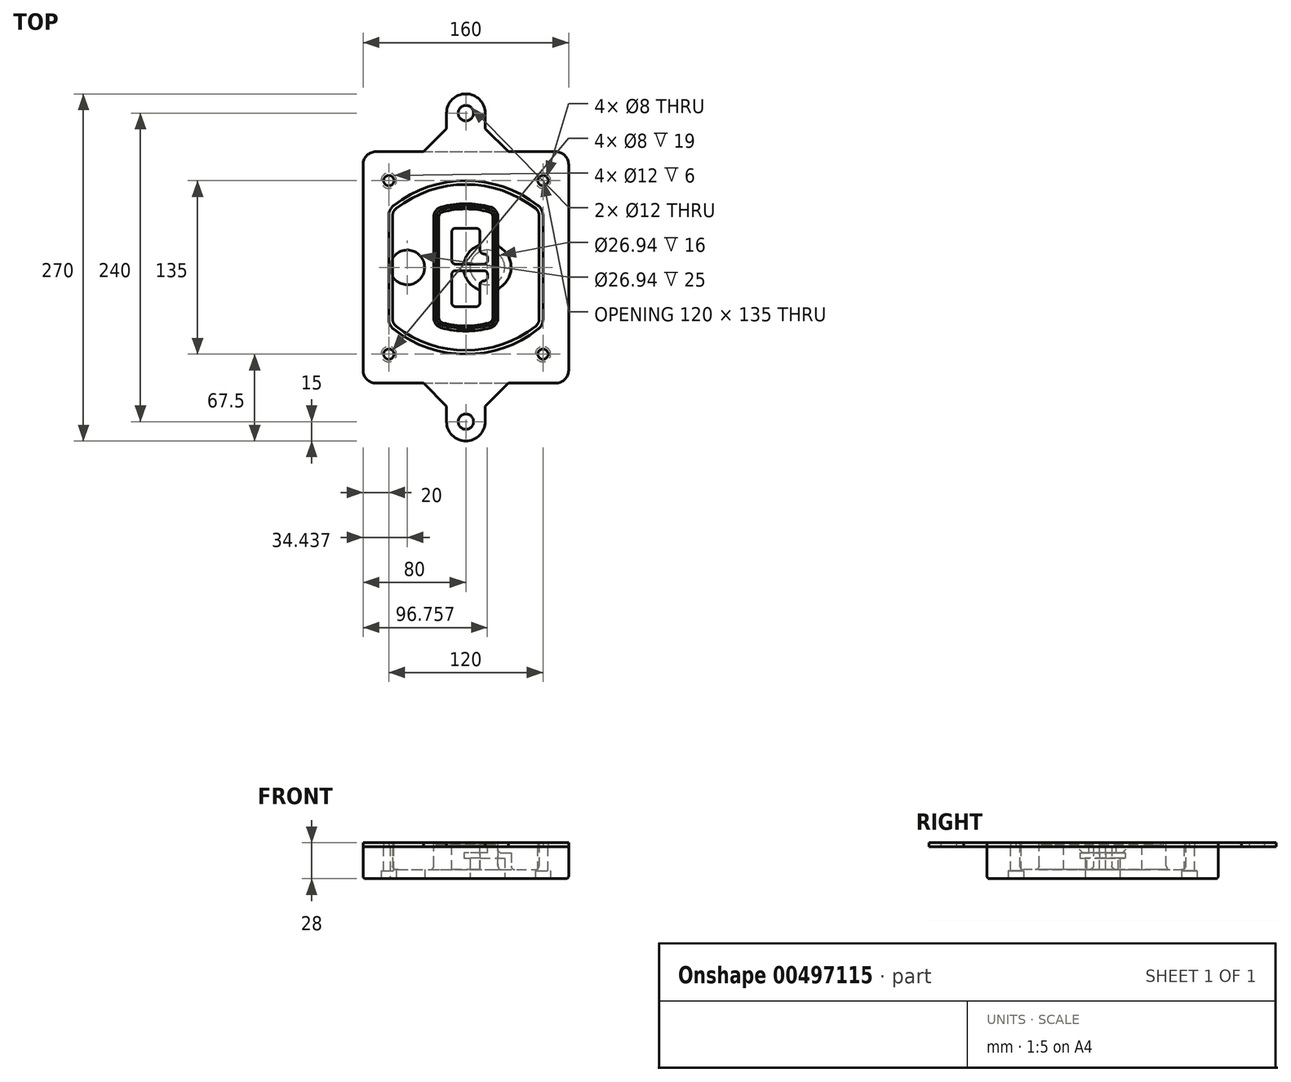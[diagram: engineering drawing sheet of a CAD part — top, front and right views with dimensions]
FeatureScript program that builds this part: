
annotation { "Feature Type Name" : "Feature", "Feature Type Description" : "" }
export const myFeature = defineFeature(function(context is Context, id is Id, definition is map)
    precondition{}
    {
        {
            var Q0;
            Q0=qCreatedBy(makeId("Top.planeOp"),FACE);
            var sketch = newSketch(context, id + "F0", { "sketchPlane" : qUnion([Q0])});
            skPoint(sketch, "E0.rect.middle", {"position": v(0, 0) * mm});
            skLineSegment(sketch, "E1.bottom", {"start": v(-70, -90) * mm, "end": v(70, -90) * mm});
            skLineSegment(sketch, "E1.top", {"start": v(-70, 90) * mm, "end": v(70, 90) * mm});
            skLineSegment(sketch, "E1.left", {"start": v(-80, -80) * mm, "end": v(-80, 80) * mm});
            skLineSegment(sketch, "E1.right", {"start": v(80, -80) * mm, "end": v(80, 80) * mm});
            skLineSegment(sketch, "E2", {"start": v(-80, 90) * mm, "end": v(80, -90) * mm, "construction": true});
            skLineSegment(sketch, "E3", {"start": v(80, 90) * mm, "end": v(-80, -90) * mm, "construction": true});
            skCircle(sketch, "E4", {"center": v(-60, 67.5) * mm, "radius": 4 * mm});
            skCircle(sketch, "E5", {"center": v(60, 67.5) * mm, "radius": 4 * mm});
            skCircle(sketch, "E6", {"center": v(60, -67.5) * mm, "radius": 4 * mm});
            skCircle(sketch, "E7", {"center": v(-60, -67.5) * mm, "radius": 4 * mm});
            skLineSegment(sketch, "E8", {"start": v(-60, 67.5) * mm, "end": v(60, 67.5) * mm, "construction": true});
            skLineSegment(sketch, "E9", {"start": v(60, 67.5) * mm, "end": v(60, -67.5) * mm, "construction": true});
            skLineSegment(sketch, "E10", {"start": v(60, -67.5) * mm, "end": v(-60, -67.5) * mm, "construction": true});
            skLineSegment(sketch, "E11", {"start": v(-60, -67.5) * mm, "end": v(-60, 67.5) * mm, "construction": true});
            skLineSegment(sketch, "E12", {"start": v(-60, 40.3) * mm, "end": v(-60, -40.3) * mm});
            skLineSegment(sketch, "E13", {"start": v(60, 40.3) * mm, "end": v(60, -40.3) * mm});
            skArc(sketch, "E14", {"start": v(56.15, 48.18) * mm, "mid": v(0, 67.5) * mm, "end": v(-56.15, 48.18) * mm});
            skArc(sketch, "E15", {"start": v(-56.15, -48.18) * mm, "mid": v(0, -67.5) * mm, "end": v(56.15, -48.18) * mm});
            skLineSegment(sketch, "E16", {"start": v(-60, 0) * mm, "end": v(60, 0) * mm, "construction": true});
            skPoint(sketch, "E17.visualSharp", {"position": v(-60, -45) * mm});
            skArc(sketch, "E17.filletArc", {"start": v(-60, -40.3) * mm, "mid": v(-58.99, -44.68) * mm, "end": v(-56.15, -48.18) * mm});
            skPoint(sketch, "E18.visualSharp", {"position": v(-60, 45) * mm});
            skArc(sketch, "E18.filletArc", {"start": v(-56.15, 48.18) * mm, "mid": v(-58.99, 44.68) * mm, "end": v(-60, 40.3) * mm});
            skPoint(sketch, "E19.visualSharp", {"position": v(60, 45) * mm});
            skArc(sketch, "E19.filletArc", {"start": v(60, 40.3) * mm, "mid": v(58.99, 44.68) * mm, "end": v(56.15, 48.18) * mm});
            skPoint(sketch, "E20.visualSharp", {"position": v(60, -45) * mm});
            skArc(sketch, "E20.filletArc", {"start": v(56.15, -48.18) * mm, "mid": v(58.99, -44.68) * mm, "end": v(60, -40.3) * mm});
            skPoint(sketch, "E21.visualSharp", {"position": v(-80, 90) * mm});
            skArc(sketch, "E21.filletArc", {"start": v(-70, 90) * mm, "mid": v(-77.07, 87.07) * mm, "end": v(-80, 80) * mm});
            skPoint(sketch, "E22.visualSharp", {"position": v(80, 90) * mm});
            skArc(sketch, "E22.filletArc", {"start": v(80, 80) * mm, "mid": v(77.07, 87.07) * mm, "end": v(70, 90) * mm});
            skPoint(sketch, "E23.visualSharp", {"position": v(80, -90) * mm});
            skArc(sketch, "E23.filletArc", {"start": v(70, -90) * mm, "mid": v(77.07, -87.07) * mm, "end": v(80, -80) * mm});
            skPoint(sketch, "E24.visualSharp", {"position": v(-80, -90) * mm});
            skArc(sketch, "E24.filletArc", {"start": v(-80, -80) * mm, "mid": v(-77.07, -87.07) * mm, "end": v(-70, -90) * mm});
            skArc(sketch, "E25.0", {"start": v(57, 40.3) * mm, "mid": v(56.3, 43.36) * mm, "end": v(54.3, 45.81) * mm});
            skLineSegment(sketch, "E25.1", {"start": v(57, 40.3) * mm, "end": v(57, -40.3) * mm});
            skArc(sketch, "E25.2", {"start": v(54.3, -45.81) * mm, "mid": v(56.3, -43.36) * mm, "end": v(57, -40.3) * mm});
            skArc(sketch, "E25.3", {"start": v(-54.3, -45.81) * mm, "mid": v(0, -64.5) * mm, "end": v(54.3, -45.81) * mm});
            skArc(sketch, "E25.4", {"start": v(-57, -40.3) * mm, "mid": v(-56.3, -43.36) * mm, "end": v(-54.3, -45.81) * mm});
            skArc(sketch, "E25.5", {"start": v(54.3, 45.81) * mm, "mid": v(0, 64.5) * mm, "end": v(-54.3, 45.81) * mm});
            skLineSegment(sketch, "E25.6", {"start": v(-57, 40.3) * mm, "end": v(-57, -40.3) * mm});
            skArc(sketch, "E25.7", {"start": v(-54.3, 45.81) * mm, "mid": v(-56.3, 43.36) * mm, "end": v(-57, 40.3) * mm});
            skArc(sketch, "E26.0", {"start": v(-58.62, 51.33) * mm, "mid": v(-62.58, 46.43) * mm, "end": v(-64, 40.3) * mm});
            skArc(sketch, "E26.1", {"start": v(58.62, 51.33) * mm, "mid": v(0, 71.5) * mm, "end": v(-58.62, 51.33) * mm});
            skArc(sketch, "E26.2", {"start": v(64, 40.3) * mm, "mid": v(62.58, 46.43) * mm, "end": v(58.62, 51.33) * mm});
            skLineSegment(sketch, "E26.3", {"start": v(64, 40.3) * mm, "end": v(64, -40.3) * mm});
            skArc(sketch, "E26.4", {"start": v(58.62, -51.33) * mm, "mid": v(62.58, -46.43) * mm, "end": v(64, -40.3) * mm});
            skLineSegment(sketch, "E26.5", {"start": v(-64, 40.3) * mm, "end": v(-64, -40.3) * mm});
            skArc(sketch, "E26.6", {"start": v(-58.62, -51.33) * mm, "mid": v(0, -71.5) * mm, "end": v(58.62, -51.33) * mm});
            skArc(sketch, "E26.7", {"start": v(-64, -40.3) * mm, "mid": v(-62.58, -46.43) * mm, "end": v(-58.62, -51.33) * mm});
            skSolve(sketch);
        }
        {
            var Q0;
            Q0=makeQuery(id+"F0.imprint","IMPRINT",FACE,{"disambiguationData":[TD([[makeQuery(id+"F0.imprint","IMPRINT",EDGE,{"derivedFrom":sQuery(id+"F0.wireOp",EDGE,"E1.bottom")}),1.0]])]});
            var Q1;
            Q1=makeQuery(id+"F0.imprint","IMPRINT",FACE,{"disambiguationData":[TD([[makeQuery(id+"F0.imprint","IMPRINT",EDGE,{"derivedFrom":sQuery(id+"F0.wireOp",EDGE,"E12")}),1.0]])]});
            var Q2;
            Q2=makeQuery(id+"F0.imprint","IMPRINT",FACE,{"disambiguationData":[TD([[makeQuery(id+"F0.imprint","IMPRINT",EDGE,{"derivedFrom":sQuery(id+"F0.wireOp",EDGE,"E25.0")}),1.0]])]});
            var Q3;
            Q3=makeQuery(id+"F0.imprint","IMPRINT",FACE,{"disambiguationData":[TD([[makeQuery(id+"F0.imprint","IMPRINT",EDGE,{"derivedFrom":sQuery(id+"F0.wireOp",EDGE,"E12")}),-1.0]])]});
            extrude(context, id + "F1", {"entities" : qUnion([Q0, Q1, Q2, Q3]), "oppositeDirection" : true, "depth" : 25 * mm});
        }
        {
            var Q0;
            Q0=makeQuery(id+"F0.imprint","IMPRINT",FACE,{"disambiguationData":[TD([[makeQuery(id+"F0.imprint","IMPRINT",EDGE,{"derivedFrom":sQuery(id+"F0.wireOp",EDGE,"E12")}),1.0]])]});
            extrude(context, id + "F2", {"entities" : qUnion([Q0]), "operationType" : NewBodyOperationType.ADD, "depth" : 3 * mm});
        }
        {
            var Q0;
            Q0=makeQuery(id+"F0.imprint","IMPRINT",FACE,{"disambiguationData":[TD([[makeQuery(id+"F0.imprint","IMPRINT",EDGE,{"derivedFrom":sQuery(id+"F0.wireOp",EDGE,"E25.0")}),1.0]])]});
            extrude(context, id + "F3", {"entities" : qUnion([Q0]), "operationType" : NewBodyOperationType.REMOVE, "oppositeDirection" : true, "depth" : 18 * mm});
        }
        {
            var Q0;
            Q0=makeQuery(id+"F2.opExtrude","CAP_FACE",FACE,{"disambiguationData":[OSD([sQuery(id+"F0.wireOp",EDGE,"E12"),sQuery(id+"F0.wireOp",EDGE,"E13"),sQuery(id+"F0.wireOp",EDGE,"E14"),sQuery(id+"F0.wireOp",EDGE,"E15"),sQuery(id+"F0.wireOp",EDGE,"E17.filletArc"),sQuery(id+"F0.wireOp",EDGE,"E18.filletArc"),sQuery(id+"F0.wireOp",EDGE,"E19.filletArc"),sQuery(id+"F0.wireOp",EDGE,"E20.filletArc"),sQuery(id+"F0.wireOp",EDGE,"E25.0"),sQuery(id+"F0.wireOp",EDGE,"E25.1"),sQuery(id+"F0.wireOp",EDGE,"E25.2"),sQuery(id+"F0.wireOp",EDGE,"E25.3"),sQuery(id+"F0.wireOp",EDGE,"E25.4"),sQuery(id+"F0.wireOp",EDGE,"E25.5"),sQuery(id+"F0.wireOp",EDGE,"E25.6"),sQuery(id+"F0.wireOp",EDGE,"E25.7")])],"isStart":false});
            var sketch = newSketch(context, id + "F4", { "sketchPlane" : qUnion([Q0])});
            skArc(sketch, "E27.0", {"start": v(-19.08, -46.97) * mm, "mid": v(0, -49.5) * mm, "end": v(19.08, -46.97) * mm});
            skArc(sketch, "E28.0", {"start": v(19.08, 46.97) * mm, "mid": v(0, 49.5) * mm, "end": v(-19.08, 46.97) * mm});
            skLineSegment(sketch, "E29", {"start": v(-25, 39.25) * mm, "end": v(-25, -39.25) * mm});
            skLineSegment(sketch, "E30", {"start": v(25, 39.25) * mm, "end": v(25, -39.25) * mm});
            skLineSegment(sketch, "E31", {"start": v(-25, 45.1) * mm, "end": v(25, 45.1) * mm, "construction": true});
            skLineSegment(sketch, "E32", {"start": v(-25, -45.1) * mm, "end": v(25, -45.1) * mm, "construction": true});
            skPoint(sketch, "E33.visualSharp", {"position": v(-25, 45.1) * mm});
            skArc(sketch, "E33.filletArc", {"start": v(-19.08, 46.97) * mm, "mid": v(-23.35, 44.11) * mm, "end": v(-25, 39.25) * mm});
            skPoint(sketch, "E34.visualSharp", {"position": v(25, 45.1) * mm});
            skArc(sketch, "E34.filletArc", {"start": v(25, 39.25) * mm, "mid": v(23.35, 44.11) * mm, "end": v(19.08, 46.97) * mm});
            skPoint(sketch, "E35.visualSharp", {"position": v(25, -45.1) * mm});
            skArc(sketch, "E35.filletArc", {"start": v(19.08, -46.97) * mm, "mid": v(23.35, -44.11) * mm, "end": v(25, -39.25) * mm});
            skPoint(sketch, "E36.visualSharp", {"position": v(-25, -45.1) * mm});
            skArc(sketch, "E36.filletArc", {"start": v(-25, -39.25) * mm, "mid": v(-23.35, -44.11) * mm, "end": v(-19.08, -46.97) * mm});
            skArc(sketch, "E37.0", {"start": v(54.3, 45.81) * mm, "mid": v(0, 64.5) * mm, "end": v(-54.3, 45.81) * mm});
            skArc(sketch, "E37.1", {"start": v(-54.3, 45.81) * mm, "mid": v(-56.3, 43.36) * mm, "end": v(-57, 40.3) * mm});
            skLineSegment(sketch, "E37.2", {"start": v(-57, 40.3) * mm, "end": v(-57, -40.3) * mm});
            skArc(sketch, "E37.3", {"start": v(-57, -40.3) * mm, "mid": v(-56.3, -43.36) * mm, "end": v(-54.3, -45.81) * mm});
            skArc(sketch, "E37.4", {"start": v(-54.3, -45.81) * mm, "mid": v(0, -64.5) * mm, "end": v(54.3, -45.81) * mm});
            skArc(sketch, "E37.5", {"start": v(54.3, -45.81) * mm, "mid": v(56.3, -43.36) * mm, "end": v(57, -40.3) * mm});
            skLineSegment(sketch, "E37.6", {"start": v(57, 40.3) * mm, "end": v(57, -40.3) * mm});
            skArc(sketch, "E37.7", {"start": v(57, 40.3) * mm, "mid": v(56.3, 43.36) * mm, "end": v(54.3, 45.81) * mm});
            skLineSegment(sketch, "E38.0", {"start": v(23, 39.25) * mm, "end": v(23, -39.25) * mm});
            skArc(sketch, "E38.1", {"start": v(18.56, -45.04) * mm, "mid": v(21.76, -42.9) * mm, "end": v(23, -39.25) * mm});
            skArc(sketch, "E38.2", {"start": v(-18.56, -45.04) * mm, "mid": v(0, -47.5) * mm, "end": v(18.56, -45.04) * mm});
            skArc(sketch, "E38.3", {"start": v(-23, -39.25) * mm, "mid": v(-21.76, -42.9) * mm, "end": v(-18.56, -45.04) * mm});
            skLineSegment(sketch, "E38.4", {"start": v(-23, 39.25) * mm, "end": v(-23, -39.25) * mm});
            skArc(sketch, "E38.5", {"start": v(23, 39.25) * mm, "mid": v(21.76, 42.9) * mm, "end": v(18.56, 45.04) * mm});
            skArc(sketch, "E38.6", {"start": v(-18.56, 45.04) * mm, "mid": v(-21.76, 42.9) * mm, "end": v(-23, 39.25) * mm});
            skArc(sketch, "E38.7", {"start": v(18.56, 45.04) * mm, "mid": v(0, 47.5) * mm, "end": v(-18.56, 45.04) * mm});
            skArc(sketch, "E39.0", {"start": v(21, 39.25) * mm, "mid": v(20.18, 41.68) * mm, "end": v(18.04, 43.1) * mm});
            skLineSegment(sketch, "E39.1", {"start": v(21, 39.25) * mm, "end": v(21, -39.25) * mm});
            skArc(sketch, "E39.2", {"start": v(18.04, -43.1) * mm, "mid": v(20.18, -41.68) * mm, "end": v(21, -39.25) * mm});
            skArc(sketch, "E39.3", {"start": v(-18.04, -43.1) * mm, "mid": v(0, -45.5) * mm, "end": v(18.04, -43.1) * mm});
            skArc(sketch, "E39.4", {"start": v(-21, -39.25) * mm, "mid": v(-20.18, -41.68) * mm, "end": v(-18.04, -43.1) * mm});
            skArc(sketch, "E39.5", {"start": v(18.04, 43.1) * mm, "mid": v(0, 45.5) * mm, "end": v(-18.04, 43.1) * mm});
            skLineSegment(sketch, "E39.6", {"start": v(-21, 39.25) * mm, "end": v(-21, -39.25) * mm});
            skArc(sketch, "E39.7", {"start": v(-18.04, 43.1) * mm, "mid": v(-20.18, 41.68) * mm, "end": v(-21, 39.25) * mm});
            skLineSegment(sketch, "E40", {"start": v(-25, 0) * mm, "end": v(25, 0) * mm, "construction": true});
            skLineSegment(sketch, "E41", {"start": v(-11, 5.5) * mm, "end": v(-11, 27.5) * mm});
            skLineSegment(sketch, "E42", {"start": v(-8, 30.5) * mm, "end": v(8, 30.5) * mm});
            skLineSegment(sketch, "E43", {"start": v(11, 27.5) * mm, "end": v(11, 13.5) * mm});
            skLineSegment(sketch, "E44", {"start": v(14, 10.5) * mm, "end": v(14, 10.5) * mm});
            skLineSegment(sketch, "E45", {"start": v(17, 7.5) * mm, "end": v(17, 5.5) * mm});
            skLineSegment(sketch, "E46", {"start": v(14, 2.5) * mm, "end": v(-8, 2.5) * mm});
            skPoint(sketch, "E47.visualSharp", {"position": v(-11, 30.5) * mm});
            skArc(sketch, "E47.filletArc", {"start": v(-8, 30.5) * mm, "mid": v(-10.12, 29.62) * mm, "end": v(-11, 27.5) * mm});
            skPoint(sketch, "E48.visualSharp", {"position": v(11, 30.5) * mm});
            skArc(sketch, "E48.filletArc", {"start": v(11, 27.5) * mm, "mid": v(10.12, 29.62) * mm, "end": v(8, 30.5) * mm});
            skPoint(sketch, "E49.visualSharp", {"position": v(11, 10.5) * mm});
            skArc(sketch, "E49.filletArc", {"start": v(11, 13.5) * mm, "mid": v(11.88, 11.38) * mm, "end": v(14, 10.5) * mm});
            skPoint(sketch, "E50.visualSharp", {"position": v(17, 10.5) * mm});
            skArc(sketch, "E50.filletArc", {"start": v(17, 7.5) * mm, "mid": v(16.12, 9.62) * mm, "end": v(14, 10.5) * mm});
            skPoint(sketch, "E51.visualSharp", {"position": v(17, 2.5) * mm});
            skArc(sketch, "E51.filletArc", {"start": v(14, 2.5) * mm, "mid": v(16.12, 3.38) * mm, "end": v(17, 5.5) * mm});
            skPoint(sketch, "E52.visualSharp", {"position": v(-11, 2.5) * mm});
            skArc(sketch, "E52.filletArc", {"start": v(-11, 5.5) * mm, "mid": v(-10.12, 3.38) * mm, "end": v(-8, 2.5) * mm});
            skLineSegment(sketch, "E53.0.MirrorCS", {"start": v(14, -2.5) * mm, "end": v(-8, -2.5) * mm});
            skArc(sketch, "E54.0.MirrorCS", {"start": v(-11, -5.5) * mm, "mid": v(-10.12, -3.38) * mm, "end": v(-8, -2.5) * mm});
            skLineSegment(sketch, "E55.0.MirrorCS", {"start": v(-11, -5.5) * mm, "end": v(-11, -27.5) * mm});
            skArc(sketch, "E56.0.MirrorCS", {"start": v(-8, -30.5) * mm, "mid": v(-10.12, -29.62) * mm, "end": v(-11, -27.5) * mm});
            skLineSegment(sketch, "E57.0.MirrorCS", {"start": v(-8, -30.5) * mm, "end": v(8, -30.5) * mm});
            skArc(sketch, "E58.0.MirrorCS", {"start": v(11, -27.5) * mm, "mid": v(10.12, -29.62) * mm, "end": v(8, -30.5) * mm});
            skLineSegment(sketch, "E59.0.MirrorCS", {"start": v(11, -27.5) * mm, "end": v(11, -13.5) * mm});
            skArc(sketch, "E60.0.MirrorCS", {"start": v(11, -13.5) * mm, "mid": v(11.88, -11.38) * mm, "end": v(14, -10.5) * mm});
            skArc(sketch, "E61.0.MirrorCS", {"start": v(17, -7.5) * mm, "mid": v(16.12, -9.62) * mm, "end": v(14, -10.5) * mm});
            skLineSegment(sketch, "E62.0.MirrorCS", {"start": v(17, -7.5) * mm, "end": v(17, -5.5) * mm});
            skArc(sketch, "E63.0.MirrorCS", {"start": v(14, -2.5) * mm, "mid": v(16.12, -3.38) * mm, "end": v(17, -5.5) * mm});
            skSolve(sketch);
        }
        {
            var Q0;
            Q0=makeQuery(id+"F4.imprint","IMPRINT",FACE,{"disambiguationData":[TD([[makeQuery(id+"F4.imprint","IMPRINT",EDGE,{"derivedFrom":sQuery(id+"F4.wireOp",EDGE,"E27.0")}),1.0]])]});
            var Q1;
            Q1=makeQuery(id+"F4.imprint","IMPRINT",FACE,{"disambiguationData":[TD([[makeQuery(id+"F4.imprint","IMPRINT",EDGE,{"derivedFrom":sQuery(id+"F4.wireOp",EDGE,"E38.0")}),-1.0]])]});
            var Q2;
            Q2=makeQuery(id+"F4.imprint","IMPRINT",FACE,{"disambiguationData":[TD([[makeQuery(id+"F4.imprint","IMPRINT",EDGE,{"derivedFrom":sQuery(id+"F4.wireOp",EDGE,"E39.0")}),1.0]])]});
            extrude(context, id + "F5", {"entities" : qUnion([Q0, Q1, Q2]), "operationType" : NewBodyOperationType.ADD, "endBound" : BoundingType.UP_TO_NEXT, "oppositeDirection" : true, "depth" : 25 * mm});
        }
        {
            var Q0;
            Q0=makeQuery(id+"F4.imprint","IMPRINT",FACE,{"disambiguationData":[TD([[makeQuery(id+"F4.imprint","IMPRINT",EDGE,{"derivedFrom":sQuery(id+"F4.wireOp",EDGE,"E38.0")}),-1.0]])]});
            extrude(context, id + "F6", {"entities" : qUnion([Q0]), "operationType" : NewBodyOperationType.REMOVE, "oppositeDirection" : true, "depth" : 2 * mm});
        }
        {
            var Q0;
            Q0=makeQuery(id+"F1.opExtrude","CAP_FACE",FACE,{"disambiguationData":[OSD([sQuery(id+"F0.wireOp",EDGE,"E1.bottom"),sQuery(id+"F0.wireOp",EDGE,"E1.top"),sQuery(id+"F0.wireOp",EDGE,"E1.left"),sQuery(id+"F0.wireOp",EDGE,"E1.right"),sQuery(id+"F0.wireOp",EDGE,"E4"),sQuery(id+"F0.wireOp",EDGE,"E5"),sQuery(id+"F0.wireOp",EDGE,"E6"),sQuery(id+"F0.wireOp",EDGE,"E7"),sQuery(id+"F0.wireOp",EDGE,"E21.filletArc"),sQuery(id+"F0.wireOp",EDGE,"E22.filletArc"),sQuery(id+"F0.wireOp",EDGE,"E23.filletArc"),sQuery(id+"F0.wireOp",EDGE,"E24.filletArc")])],"isStart":false});
            var sketch = newSketch(context, id + "F7", { "sketchPlane" : qUnion([Q0])});
            skCircle(sketch, "E64", {"center": v(16.76, 0) * mm, "radius": 13.47 * mm});
            skCircle(sketch, "E65", {"center": v(-45.56, 0) * mm, "radius": 13.47 * mm});
            skLineSegment(sketch, "E66", {"start": v(80, 0) * mm, "end": v(-80, 0) * mm});
            skCircle(sketch, "E67", {"center": v(16.76, 0) * mm, "radius": 18.47 * mm});
            skCircle(sketch, "E68", {"center": v(60, -67.5) * mm, "radius": 6 * mm});
            skCircle(sketch, "E69", {"center": v(-60, -67.5) * mm, "radius": 6 * mm});
            skCircle(sketch, "E70", {"center": v(-60, 67.5) * mm, "radius": 6 * mm});
            skCircle(sketch, "E71", {"center": v(60, 67.5) * mm, "radius": 6 * mm});
            skSolve(sketch);
        }
        {
            var Q0;
            {var subQ1=sQuery(id+"F7.wireOp",EDGE,"E66");var subQ4=sQuery(id+"F7.wireOp",EDGE,"E64");var subQ6=makeQuery(id+"F7.imprint","INTERSECT",VERTEX,{"disambiguationData":[OD(0.0)],"derivedFrom":[subQ4,subQ1]});Q0=makeQuery(id+"F7.imprint","IMPRINT",FACE,{"disambiguationData":[TD([[makeQuery(id+"F7.imprint","IMPRINT",EDGE,{"disambiguationData":[TD([[subQ6,-1.0]])],"derivedFrom":subQ4}),-1.0]])]});}
            var Q1;
            {var subQ0=sQuery(id+"F7.wireOp",EDGE,"E66");var subQ1=sQuery(id+"F7.wireOp",EDGE,"E64");var subQ3=makeQuery(id+"F7.imprint","INTERSECT",VERTEX,{"disambiguationData":[OD(0.0)],"derivedFrom":[subQ1,subQ0]});Q1=makeQuery(id+"F7.imprint","IMPRINT",FACE,{"disambiguationData":[TD([[makeQuery(id+"F7.imprint","IMPRINT",EDGE,{"disambiguationData":[TD([[subQ3,-1.0]])],"derivedFrom":subQ1}),1.0]])]});}
            var Q2;
            {var subQ0=sQuery(id+"F7.wireOp",EDGE,"E66");var subQ1=sQuery(id+"F7.wireOp",EDGE,"E64");var subQ3=makeQuery(id+"F7.imprint","INTERSECT",VERTEX,{"disambiguationData":[OD(0.0)],"derivedFrom":[subQ1,subQ0]});Q2=makeQuery(id+"F7.imprint","IMPRINT",FACE,{"disambiguationData":[TD([[makeQuery(id+"F7.imprint","IMPRINT",EDGE,{"disambiguationData":[TD([[subQ3,1.0]])],"derivedFrom":subQ1}),1.0]])]});}
            var Q3;
            {var subQ1=sQuery(id+"F7.wireOp",EDGE,"E66");var subQ4=sQuery(id+"F7.wireOp",EDGE,"E64");var subQ6=makeQuery(id+"F7.imprint","INTERSECT",VERTEX,{"disambiguationData":[OD(0.0)],"derivedFrom":[subQ4,subQ1]});Q3=makeQuery(id+"F7.imprint","IMPRINT",FACE,{"disambiguationData":[TD([[makeQuery(id+"F7.imprint","IMPRINT",EDGE,{"disambiguationData":[TD([[subQ6,1.0]])],"derivedFrom":subQ4}),-1.0]])]});}
            extrude(context, id + "F8", {"entities" : qUnion([Q0, Q1, Q2, Q3]), "operationType" : NewBodyOperationType.ADD, "oppositeDirection" : true, "depth" : 20 * mm});
        }
        {
            var Q0;
            {var subQ0=sQuery(id+"F7.wireOp",EDGE,"E66");var subQ1=sQuery(id+"F7.wireOp",EDGE,"E64");var subQ3=makeQuery(id+"F7.imprint","INTERSECT",VERTEX,{"disambiguationData":[OD(0.0)],"derivedFrom":[subQ1,subQ0]});Q0=makeQuery(id+"F7.imprint","IMPRINT",FACE,{"disambiguationData":[TD([[makeQuery(id+"F7.imprint","IMPRINT",EDGE,{"disambiguationData":[TD([[subQ3,-1.0]])],"derivedFrom":subQ1}),1.0]])]});}
            var Q1;
            {var subQ0=sQuery(id+"F7.wireOp",EDGE,"E66");var subQ1=sQuery(id+"F7.wireOp",EDGE,"E64");var subQ3=makeQuery(id+"F7.imprint","INTERSECT",VERTEX,{"disambiguationData":[OD(0.0)],"derivedFrom":[subQ1,subQ0]});Q1=makeQuery(id+"F7.imprint","IMPRINT",FACE,{"disambiguationData":[TD([[makeQuery(id+"F7.imprint","IMPRINT",EDGE,{"disambiguationData":[TD([[subQ3,1.0]])],"derivedFrom":subQ1}),1.0]])]});}
            extrude(context, id + "F9", {"entities" : qUnion([Q0, Q1]), "operationType" : NewBodyOperationType.REMOVE, "oppositeDirection" : true, "depth" : 16 * mm});
        }
        {
            var Q0;
            {var subQ0=sQuery(id+"F7.wireOp",EDGE,"E66");var subQ1=sQuery(id+"F7.wireOp",EDGE,"E65");var subQ3=makeQuery(id+"F7.imprint","INTERSECT",VERTEX,{"disambiguationData":[OD(0.0)],"derivedFrom":[subQ1,subQ0]});Q0=makeQuery(id+"F7.imprint","IMPRINT",FACE,{"disambiguationData":[TD([[makeQuery(id+"F7.imprint","IMPRINT",EDGE,{"disambiguationData":[TD([[subQ3,-1.0]])],"derivedFrom":subQ1}),1.0]])]});}
            var Q1;
            {var subQ0=sQuery(id+"F7.wireOp",EDGE,"E66");var subQ1=sQuery(id+"F7.wireOp",EDGE,"E65");var subQ3=makeQuery(id+"F7.imprint","INTERSECT",VERTEX,{"disambiguationData":[OD(0.0)],"derivedFrom":[subQ1,subQ0]});Q1=makeQuery(id+"F7.imprint","IMPRINT",FACE,{"disambiguationData":[TD([[makeQuery(id+"F7.imprint","IMPRINT",EDGE,{"disambiguationData":[TD([[subQ3,1.0]])],"derivedFrom":subQ1}),1.0]])]});}
            extrude(context, id + "F10", {"entities" : qUnion([Q0, Q1]), "operationType" : NewBodyOperationType.REMOVE, "oppositeDirection" : true, "depth" : 25 * mm});
        }
        {
            var Q0;
            Q0=makeQuery(id+"F7.imprint","IMPRINT",FACE,{"disambiguationData":[TD([[makeQuery(id+"F7.imprint","IMPRINT",EDGE,{"derivedFrom":sQuery(id+"F7.wireOp",EDGE,"E68")}),1.0]])]});
            var Q1;
            Q1=makeQuery(id+"F7.imprint","IMPRINT",FACE,{"disambiguationData":[TD([[makeQuery(id+"F7.imprint","IMPRINT",EDGE,{"derivedFrom":makeQuery(id+"F1.opExtrude","CAP_EDGE",EDGE,{"disambiguationData":[OSD([sQuery(id+"F0.wireOp",EDGE,"E5")])],"isStart":false})}),-1.0]])]});
            var Q2;
            Q2=makeQuery(id+"F7.imprint","IMPRINT",FACE,{"disambiguationData":[TD([[makeQuery(id+"F7.imprint","IMPRINT",EDGE,{"derivedFrom":sQuery(id+"F7.wireOp",EDGE,"E69")}),1.0]])]});
            var Q3;
            Q3=makeQuery(id+"F7.imprint","IMPRINT",FACE,{"disambiguationData":[TD([[makeQuery(id+"F7.imprint","IMPRINT",EDGE,{"derivedFrom":makeQuery(id+"F1.opExtrude","CAP_EDGE",EDGE,{"disambiguationData":[OSD([sQuery(id+"F0.wireOp",EDGE,"E4")])],"isStart":false})}),-1.0]])]});
            var Q4;
            Q4=makeQuery(id+"F7.imprint","IMPRINT",FACE,{"disambiguationData":[TD([[makeQuery(id+"F7.imprint","IMPRINT",EDGE,{"derivedFrom":sQuery(id+"F7.wireOp",EDGE,"E70")}),1.0]])]});
            var Q5;
            Q5=makeQuery(id+"F7.imprint","IMPRINT",FACE,{"disambiguationData":[TD([[makeQuery(id+"F7.imprint","IMPRINT",EDGE,{"derivedFrom":makeQuery(id+"F1.opExtrude","CAP_EDGE",EDGE,{"disambiguationData":[OSD([sQuery(id+"F0.wireOp",EDGE,"E7")])],"isStart":false})}),-1.0]])]});
            var Q6;
            Q6=makeQuery(id+"F7.imprint","IMPRINT",FACE,{"disambiguationData":[TD([[makeQuery(id+"F7.imprint","IMPRINT",EDGE,{"derivedFrom":sQuery(id+"F7.wireOp",EDGE,"E71")}),1.0]])]});
            var Q7;
            Q7=makeQuery(id+"F7.imprint","IMPRINT",FACE,{"disambiguationData":[TD([[makeQuery(id+"F7.imprint","IMPRINT",EDGE,{"derivedFrom":makeQuery(id+"F1.opExtrude","CAP_EDGE",EDGE,{"disambiguationData":[OSD([sQuery(id+"F0.wireOp",EDGE,"E6")])],"isStart":false})}),-1.0]])]});
            extrude(context, id + "F11", {"entities" : qUnion([Q0, Q1, Q2, Q3, Q4, Q5, Q6, Q7]), "operationType" : NewBodyOperationType.REMOVE, "oppositeDirection" : true, "depth" : 6 * mm});
        }
        {
            var Q0;
            Q0=makeQuery(id+"F9.boolean.opBoolean","COPY",FACE,{"derivedFrom":makeQuery(id+"F9.opExtrude","CAP_FACE",FACE,{"disambiguationData":[OSD([sQuery(id+"F7.wireOp",EDGE,"E64")])],"isStart":false})});
            var sketch = newSketch(context, id + "F12", { "sketchPlane" : qUnion([Q0])});
            skArc(sketch, "E72.0", {"start": v(11, 17.55) * mm, "mid": v(2.57, 11.82) * mm, "end": v(-1.54, 2.5) * mm});
            skArc(sketch, "E72.1", {"start": v(-1.54, -2.5) * mm, "mid": v(2.57, -11.82) * mm, "end": v(11, -17.55) * mm});
            skLineSegment(sketch, "E73", {"start": v(-1.54, -2.5) * mm, "end": v(14, -2.5) * mm});
            skLineSegment(sketch, "E74.0", {"start": v(14, 2.5) * mm, "end": v(-1.54, 2.5) * mm});
            skArc(sketch, "E74.1", {"start": v(14, 2.5) * mm, "mid": v(16.12, 3.38) * mm, "end": v(17, 5.5) * mm});
            skLineSegment(sketch, "E74.2", {"start": v(17, 7.5) * mm, "end": v(17, 5.5) * mm});
            skArc(sketch, "E74.3", {"start": v(17, 7.5) * mm, "mid": v(16.12, 9.62) * mm, "end": v(14, 10.5) * mm});
            skArc(sketch, "E74.4", {"start": v(11, 13.5) * mm, "mid": v(11.88, 11.38) * mm, "end": v(14, 10.5) * mm});
            skLineSegment(sketch, "E74.5", {"start": v(11, 17.55) * mm, "end": v(11, 13.5) * mm});
            skLineSegment(sketch, "E74.7", {"start": v(14, -2.5) * mm, "end": v(-1.54, -2.5) * mm});
            skArc(sketch, "E74.8", {"start": v(14, -2.5) * mm, "mid": v(16.12, -3.38) * mm, "end": v(17, -5.5) * mm});
            skLineSegment(sketch, "E74.9", {"start": v(17, -7.5) * mm, "end": v(17, -5.5) * mm});
            skArc(sketch, "E74.10", {"start": v(17, -7.5) * mm, "mid": v(16.12, -9.62) * mm, "end": v(14, -10.5) * mm});
            skArc(sketch, "E74.11", {"start": v(11, -13.5) * mm, "mid": v(11.88, -11.38) * mm, "end": v(14, -10.5) * mm});
            skLineSegment(sketch, "E74.12", {"start": v(11, -17.55) * mm, "end": v(11, -13.5) * mm});
            skPoint(sketch, "E75.orphan", {"position": v(11, -27.5) * mm});
            skPoint(sketch, "E76.orphan", {"position": v(-8, -2.5) * mm});
            skPoint(sketch, "E77.orphan", {"position": v(-8, 2.5) * mm});
            skPoint(sketch, "E78.orphan", {"position": v(11, 27.5) * mm});
            skSolve(sketch);
        }
        {
            var Q0;
            {var subQ7=sQuery(id+"F12.wireOp",EDGE,"E72.0");var subQ14=sQuery(id+"F12.wireOp",EDGE,"E72.1");var subQ16=sQuery(id+"F12.wireOp",EDGE,"E74.1");var subQ18=sQuery(id+"F12.wireOp",EDGE,"E74.8");Q0=qUnion([makeQuery(id+"F12.imprint","IMPRINT",FACE,{"disambiguationData":[TD([[makeQuery(id+"F12.imprint","IMPRINT",EDGE,{"derivedFrom":subQ7}),1.0]])]}),makeQuery(id+"F12.imprint","IMPRINT",FACE,{"disambiguationData":[TD([[makeQuery(id+"F12.imprint","IMPRINT",EDGE,{"derivedFrom":subQ14}),1.0]])]}),makeQuery(id+"F12.imprint","IMPRINT",FACE,{"disambiguationData":[TD([[makeQuery(id+"F12.imprint","IMPRINT",EDGE,{"derivedFrom":subQ16}),1.0]])]}),makeQuery(id+"F12.imprint","IMPRINT",FACE,{"disambiguationData":[TD([[makeQuery(id+"F12.imprint","IMPRINT",EDGE,{"derivedFrom":subQ18}),-1.0]])]})]);}
            var Q1;
            Q1=makeQuery(id+"F5.boolean.opBoolean","SPLIT",FACE,{"disambiguationData":[TD([makeQuery(id+"F5.opExtrude","SWEPT_FACE",FACE,{"disambiguationData":[OSD([sQuery(id+"F4.wireOp",EDGE,"E41")])]})])],"derivedFrom":makeQuery(id+"F3.boolean.opBoolean","COPY",FACE,{"derivedFrom":makeQuery(id+"F3.opExtrude","CAP_FACE",FACE,{"disambiguationData":[OSD([sQuery(id+"F0.wireOp",EDGE,"E25.0"),sQuery(id+"F0.wireOp",EDGE,"E25.1"),sQuery(id+"F0.wireOp",EDGE,"E25.2"),sQuery(id+"F0.wireOp",EDGE,"E25.3"),sQuery(id+"F0.wireOp",EDGE,"E25.4"),sQuery(id+"F0.wireOp",EDGE,"E25.5"),sQuery(id+"F0.wireOp",EDGE,"E25.6"),sQuery(id+"F0.wireOp",EDGE,"E25.7")])],"isStart":false})})});
            extrude(context, id + "F13", {"entities" : qUnion([Q0]), "operationType" : NewBodyOperationType.REMOVE, "endBound" : BoundingType.UP_TO_SURFACE, "endBoundEntityFace" : qUnion([Q1]), "depth" : 25 * mm});
        }
        {
            var Q0;
            Q0=makeQuery(id+"F3.boolean.opBoolean","COPY",EDGE,{"derivedFrom":makeQuery(id+"F3.opExtrude","CAP_EDGE",EDGE,{"disambiguationData":[OSD([sQuery(id+"F0.wireOp",EDGE,"E25.6")])],"isStart":false})});
            var Q1;
            Q1=makeQuery(id+"F8.boolean.opBoolean","INTERSECT",EDGE,{"derivedFrom":[makeQuery(id+"F5.opExtrude","SWEPT_FACE",FACE,{"disambiguationData":[OSD([sQuery(id+"F4.wireOp",EDGE,"E30")])]}),makeQuery(id+"F8.opExtrude","CAP_FACE",FACE,{"disambiguationData":[OSD([sQuery(id+"F7.wireOp",EDGE,"E67")])],"isStart":false})]});
            var Q2;
            Q2=makeQuery(id+"F8.boolean.opBoolean","INTERSECT",EDGE,{"disambiguationData":[OD(1.0)],"derivedFrom":[makeQuery(id+"F5.opExtrude","SWEPT_FACE",FACE,{"disambiguationData":[OSD([sQuery(id+"F4.wireOp",EDGE,"E30")])]}),makeQuery(id+"F8.opExtrude","SWEPT_FACE",FACE,{"disambiguationData":[OSD([sQuery(id+"F7.wireOp",EDGE,"E67")])]})]});
            var Q3;
            {var subQ0=sQuery(id+"F4.wireOp",EDGE,"E30");Q3=makeQuery(id+"F8.boolean.opBoolean","SPLIT",EDGE,{"disambiguationData":[TD([makeQuery(id+"F5.opExtrude","SWEPT_FACE",FACE,{"disambiguationData":[OSD([sQuery(id+"F4.wireOp",EDGE,"E35.filletArc")])]})])],"derivedFrom":makeQuery(id+"F5.opExtrude","CAP_EDGE",EDGE,{"disambiguationData":[OSD([subQ0])],"isStart":false})});}
            var Q4;
            {var subQ0=sQuery(id+"F0.wireOp",EDGE,"E25.7");var subQ1=sQuery(id+"F0.wireOp",EDGE,"E25.1");var subQ2=sQuery(id+"F0.wireOp",EDGE,"E25.6");var subQ3=sQuery(id+"F0.wireOp",EDGE,"E25.5");var subQ4=sQuery(id+"F0.wireOp",EDGE,"E25.4");var subQ5=sQuery(id+"F0.wireOp",EDGE,"E25.0");var subQ6=sQuery(id+"F0.wireOp",EDGE,"E25.2");var subQ7=sQuery(id+"F0.wireOp",EDGE,"E25.3");Q4=makeQuery(id+"F8.boolean.opBoolean","INTERSECT",EDGE,{"derivedFrom":[makeQuery(id+"F5.boolean.opBoolean","SPLIT",FACE,{"disambiguationData":[TD([makeQuery(id+"F2.opExtrude","SWEPT_FACE",FACE,{"disambiguationData":[OSD([subQ5])]})])],"derivedFrom":makeQuery(id+"F3.boolean.opBoolean","COPY",FACE,{"derivedFrom":makeQuery(id+"F3.opExtrude","CAP_FACE",FACE,{"disambiguationData":[OSD([subQ5,subQ1,subQ6,subQ7,subQ4,subQ3,subQ2,subQ0])],"isStart":false})})}),makeQuery(id+"F8.opExtrude","SWEPT_FACE",FACE,{"disambiguationData":[OSD([sQuery(id+"F7.wireOp",EDGE,"E67")])]})]});}
            var Q5;
            Q5=makeQuery(id+"F8.boolean.opBoolean","INTERSECT",EDGE,{"disambiguationData":[OD(0.0)],"derivedFrom":[makeQuery(id+"F5.opExtrude","SWEPT_FACE",FACE,{"disambiguationData":[OSD([sQuery(id+"F4.wireOp",EDGE,"E30")])]}),makeQuery(id+"F8.opExtrude","SWEPT_FACE",FACE,{"disambiguationData":[OSD([sQuery(id+"F7.wireOp",EDGE,"E67")])]})]});
            fillet(context, id + "F14", {"entities" : qUnion([Q0, Q1, Q2, Q3, Q4, Q5]), "radius" : 3 * mm, "tangentPropagation" : true, "allowEdgeOverflow" : false});
        }
        {
            var Q0;
            Q0=makeQuery(id+"F1.opExtrude","CAP_EDGE",EDGE,{"disambiguationData":[OSD([sQuery(id+"F0.wireOp",EDGE,"E1.bottom")])],"isStart":false});
            fillet(context, id + "F15", {"entities" : qUnion([Q0]), "radius" : 2 * mm, "tangentPropagation" : true, "allowEdgeOverflow" : false});
        }
        {
            var Q0;
            {var subQ0=sQuery(id+"F0.wireOp",EDGE,"E21.filletArc");var subQ1=sQuery(id+"F0.wireOp",EDGE,"E7");var subQ2=sQuery(id+"F0.wireOp",EDGE,"E6");var subQ3=sQuery(id+"F0.wireOp",EDGE,"E5");var subQ4=sQuery(id+"F0.wireOp",EDGE,"E4");var subQ5=sQuery(id+"F0.wireOp",EDGE,"E22.filletArc");var subQ6=sQuery(id+"F0.wireOp",EDGE,"E1.bottom");var subQ7=sQuery(id+"F0.wireOp",EDGE,"E1.right");var subQ8=sQuery(id+"F0.wireOp",EDGE,"E1.top");var subQ9=sQuery(id+"F0.wireOp",EDGE,"E1.left");var subQ10=sQuery(id+"F0.wireOp",EDGE,"E23.filletArc");var subQ11=sQuery(id+"F0.wireOp",EDGE,"E24.filletArc");Q0=makeQuery(id+"F2.boolean.opBoolean","SPLIT",FACE,{"disambiguationData":[TD([makeQuery(id+"F1.opExtrude","SWEPT_FACE",FACE,{"disambiguationData":[OSD([subQ6])]})])],"derivedFrom":makeQuery(id+"F1.opExtrude","CAP_FACE",FACE,{"disambiguationData":[OSD([subQ6,subQ8,subQ9,subQ7,subQ4,subQ3,subQ2,subQ1,subQ0,subQ5,subQ10,subQ11])],"isStart":true})});}
            var sketch = newSketch(context, id + "F16", { "sketchPlane" : qUnion([Q0])});
            skLineSegment(sketch, "E79.0", {"start": v(-60, 40.3) * mm, "end": v(-60, -40.3) * mm});
            skArc(sketch, "E79.1", {"start": v(56.15, 48.18) * mm, "mid": v(0, 67.5) * mm, "end": v(-56.15, 48.18) * mm});
            skArc(sketch, "E79.2", {"start": v(-56.15, 48.18) * mm, "mid": v(-58.99, 44.68) * mm, "end": v(-60, 40.3) * mm});
            skArc(sketch, "E79.3", {"start": v(-56.15, -48.18) * mm, "mid": v(0, -67.5) * mm, "end": v(56.15, -48.18) * mm});
            skArc(sketch, "E79.4", {"start": v(56.15, -48.18) * mm, "mid": v(58.99, -44.68) * mm, "end": v(60, -40.3) * mm});
            skLineSegment(sketch, "E79.5", {"start": v(60, 40.3) * mm, "end": v(60, -40.3) * mm});
            skArc(sketch, "E79.6", {"start": v(60, 40.3) * mm, "mid": v(58.99, 44.68) * mm, "end": v(56.15, 48.18) * mm});
            skCircle(sketch, "E79.7", {"center": v(-60, 67.5) * mm, "radius": 4 * mm});
            skCircle(sketch, "E79.8", {"center": v(60, 67.5) * mm, "radius": 4 * mm});
            skCircle(sketch, "E79.9", {"center": v(60, -67.5) * mm, "radius": 4 * mm});
            skCircle(sketch, "E79.10", {"center": v(-60, -67.5) * mm, "radius": 4 * mm});
            skLineSegment(sketch, "E79.11", {"start": v(-80, -80) * mm, "end": v(-80, 80) * mm});
            skArc(sketch, "E79.12", {"start": v(-80, -80) * mm, "mid": v(-77.07, -87.07) * mm, "end": v(-70, -90) * mm});
            skLineSegment(sketch, "E79.13", {"start": v(-70, -90) * mm, "end": v(70, -90) * mm});
            skArc(sketch, "E79.14", {"start": v(70, -90) * mm, "mid": v(77.07, -87.07) * mm, "end": v(80, -80) * mm});
            skLineSegment(sketch, "E79.15", {"start": v(80, -80) * mm, "end": v(80, 80) * mm});
            skArc(sketch, "E79.16", {"start": v(80, 80) * mm, "mid": v(77.07, 87.07) * mm, "end": v(70, 90) * mm});
            skLineSegment(sketch, "E79.17", {"start": v(-70, 90) * mm, "end": v(70, 90) * mm});
            skArc(sketch, "E79.18", {"start": v(-70, 90) * mm, "mid": v(-77.07, 87.07) * mm, "end": v(-80, 80) * mm});
            skArc(sketch, "E79.19", {"start": v(-60, -40.3) * mm, "mid": v(-58.99, -44.68) * mm, "end": v(-56.15, -48.18) * mm});
            skCircle(sketch, "E80", {"center": v(0, 120) * mm, "radius": 6 * mm});
            skArc(sketch, "E81", {"start": v(15, 120) * mm, "mid": v(0, 135) * mm, "end": v(-15, 120) * mm});
            skLineSegment(sketch, "E82", {"start": v(0, 120) * mm, "end": v(0, 90) * mm, "construction": true});
            skPoint(sketch, "E83.endSnap0", {"position": v(0, 105) * mm});
            skLineSegment(sketch, "E84", {"start": v(-15, 120) * mm, "end": v(-15, 108) * mm});
            skLineSegment(sketch, "E85", {"start": v(33, 90) * mm, "end": v(15, 108) * mm});
            skLineSegment(sketch, "E86", {"start": v(-15, 108) * mm, "end": v(-33, 90) * mm});
            skLineSegment(sketch, "E87", {"start": v(15, 108) * mm, "end": v(15, 120) * mm});
            skPoint(sketch, "E88", {"position": v(-80, 0) * mm});
            skPoint(sketch, "E89", {"position": v(80, 0) * mm});
            skLineSegment(sketch, "E90", {"start": v(-80, 0) * mm, "end": v(80, 0) * mm, "construction": true});
            skCircle(sketch, "E91.MirrorC", {"center": v(0, -120) * mm, "radius": 6 * mm});
            skLineSegment(sketch, "E92.MirrorCS", {"start": v(-15, -120) * mm, "end": v(-15, -108) * mm});
            skLineSegment(sketch, "E93.MirrorCS", {"start": v(15, -108) * mm, "end": v(15, -120) * mm});
            skArc(sketch, "E94.MirrorCS", {"start": v(15, -120) * mm, "mid": v(0, -135) * mm, "end": v(-15, -120) * mm});
            skPoint(sketch, "E95.MirrorP", {"position": v(0, -105) * mm});
            skLineSegment(sketch, "E96.MirrorCS", {"start": v(-15, -108) * mm, "end": v(-33, -90) * mm});
            skLineSegment(sketch, "E97.MirrorCS", {"start": v(33, -90) * mm, "end": v(15, -108) * mm});
            skLineSegment(sketch, "E98.MirrorCS", {"start": v(0, -120) * mm, "end": v(0, -90) * mm, "construction": true});
            skSolve(sketch);
        }
        {
            var Q0;
            Q0 = qSketchRegion(id + "F16", true);
            var Q1;
            Q1=makeQuery(id+"F2.opExtrude","CAP_FACE",FACE,{"disambiguationData":[OSD([sQuery(id+"F0.wireOp",EDGE,"E12"),sQuery(id+"F0.wireOp",EDGE,"E13"),sQuery(id+"F0.wireOp",EDGE,"E14"),sQuery(id+"F0.wireOp",EDGE,"E15"),sQuery(id+"F0.wireOp",EDGE,"E17.filletArc"),sQuery(id+"F0.wireOp",EDGE,"E18.filletArc"),sQuery(id+"F0.wireOp",EDGE,"E19.filletArc"),sQuery(id+"F0.wireOp",EDGE,"E20.filletArc"),sQuery(id+"F0.wireOp",EDGE,"E25.0"),sQuery(id+"F0.wireOp",EDGE,"E25.1"),sQuery(id+"F0.wireOp",EDGE,"E25.2"),sQuery(id+"F0.wireOp",EDGE,"E25.3"),sQuery(id+"F0.wireOp",EDGE,"E25.4"),sQuery(id+"F0.wireOp",EDGE,"E25.5"),sQuery(id+"F0.wireOp",EDGE,"E25.6"),sQuery(id+"F0.wireOp",EDGE,"E25.7")])],"isStart":false});
            extrude(context, id + "F17", {"entities" : qUnion([Q0]), "endBound" : BoundingType.UP_TO_SURFACE, "endBoundEntityFace" : qUnion([Q1]), "depth" : 25 * mm});
        }
    });
